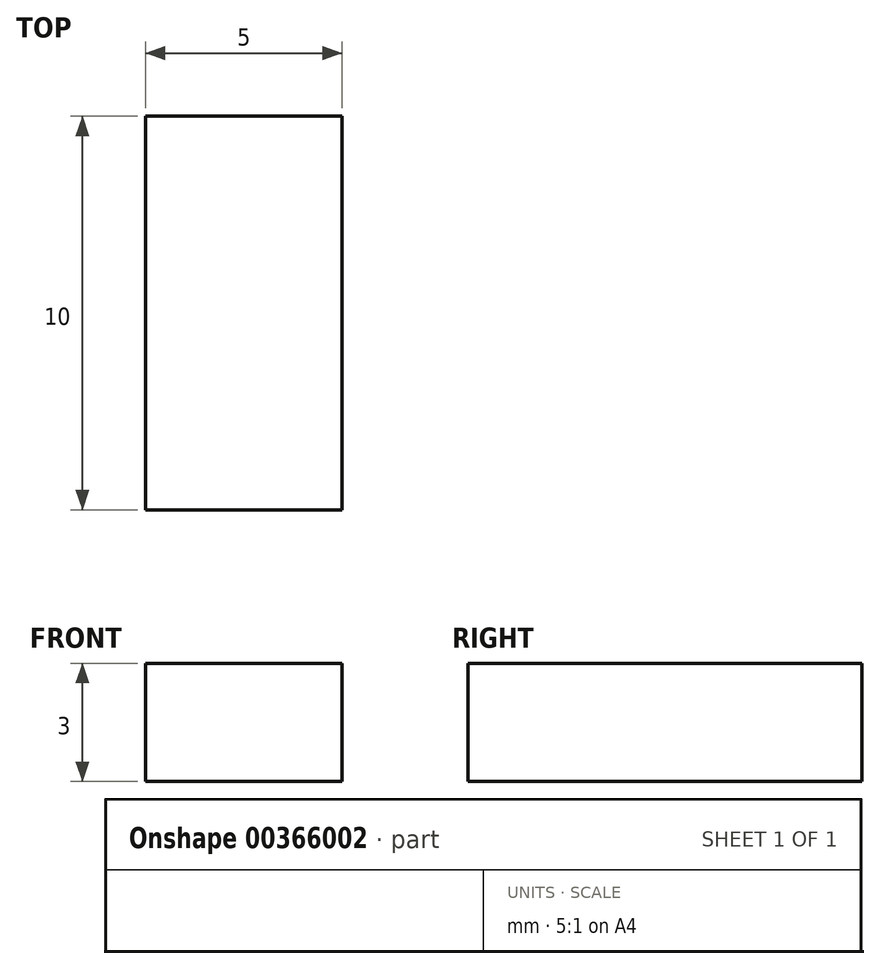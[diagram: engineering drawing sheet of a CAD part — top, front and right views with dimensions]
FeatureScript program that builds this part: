
annotation { "Feature Type Name" : "Feature", "Feature Type Description" : "" }
export const myFeature = defineFeature(function(context is Context, id is Id, definition is map)
    precondition{}
    {
        {
            var Q0;
            Q0=qCreatedBy(makeId("Front.planeOp"),FACE);
            var sketch = newSketch(context, id + "F0", { "sketchPlane" : qUnion([Q0])});
            skLineSegment(sketch, "E0.bottom", {"start": v(0, 0) * mm, "end": v(5, 0) * mm});
            skLineSegment(sketch, "E0.top", {"start": v(0, 3) * mm, "end": v(5, 3) * mm});
            skLineSegment(sketch, "E0.left", {"start": v(0, 0) * mm, "end": v(0, 3) * mm});
            skLineSegment(sketch, "E0.right", {"start": v(5, 0) * mm, "end": v(5, 3) * mm});
            skSolve(sketch);
        }
        {
            var Q0;
            Q0 = qSketchRegion(id + "F0", true);
            extrude(context, id + "F1", {"entities" : qUnion([Q0]), "depth" : 10 * mm});
        }
    });
